# Revit family: Light-BigAssFan-Haiku-Series
name_source: partatom
category: Electrical Fixtures
revit_build: Autodesk Revit MEP 2012 (Build: 20110916_2132(x64)
units: mm (PartAtom-declared; Revit-internal decimal feet)

## types (2) — shared parameters
Ambient Operating Temperature = 104° F (40° C)
Amperage = 0.12 – 0.17 A
CRI = 85.8
Controller = Haiku Home App; Handheld Remote Supplied
Default Elevation = 0"
Description = Haiku Light
Diameter = 9 179/256"
Dimming = 0–97.5%
Efficacy = 67 lm/W
Environment = Indoor And Covered Outdoor Use
IP rating = IP52
Light = Bulb - Big Ass Fan - White
Lumens = 1378 lm
Manufacturer = Big Ass Fans
Mounting = Recessed Can Housing Or Outlet Box
Power Input = 100–277 V
Product Page URL = https://www.haikuhome.com
Revit Object Download Link = http://library.smartbim.com
Sensors = Occupancy And Temperature
URL = http://www.bigassfans.com
Warranty = 5 years
Wattage Max = 21 W
Wattage Min = 21 W
Weight = 2.30 lb

## per-type parameters (varying)
| type | Color Temperature | Finishes | Model Number | Units |
| Premier Model | 2200–5000 K | Polished Aluminum,Oil-Rubbed Bronze,Satin Nickel,Black,White | 10R-01-01-A0-A-01-1.2-01-XXX-HKL | Metal - Big Ass Fan - Black |
| Select Model | 2700 K | Black,White | 10R-01-01-A0-F-02-1.2-01-XXX-HKL | Metal - Big Ass Fan - Oil-Rubbed - Bronze |

note: column(s) folded — value = type name in every type: Model

## geometry (parser evidence)
native form markers: Blend x5, Sweep x2
no freeform markers — native parametric forms only
